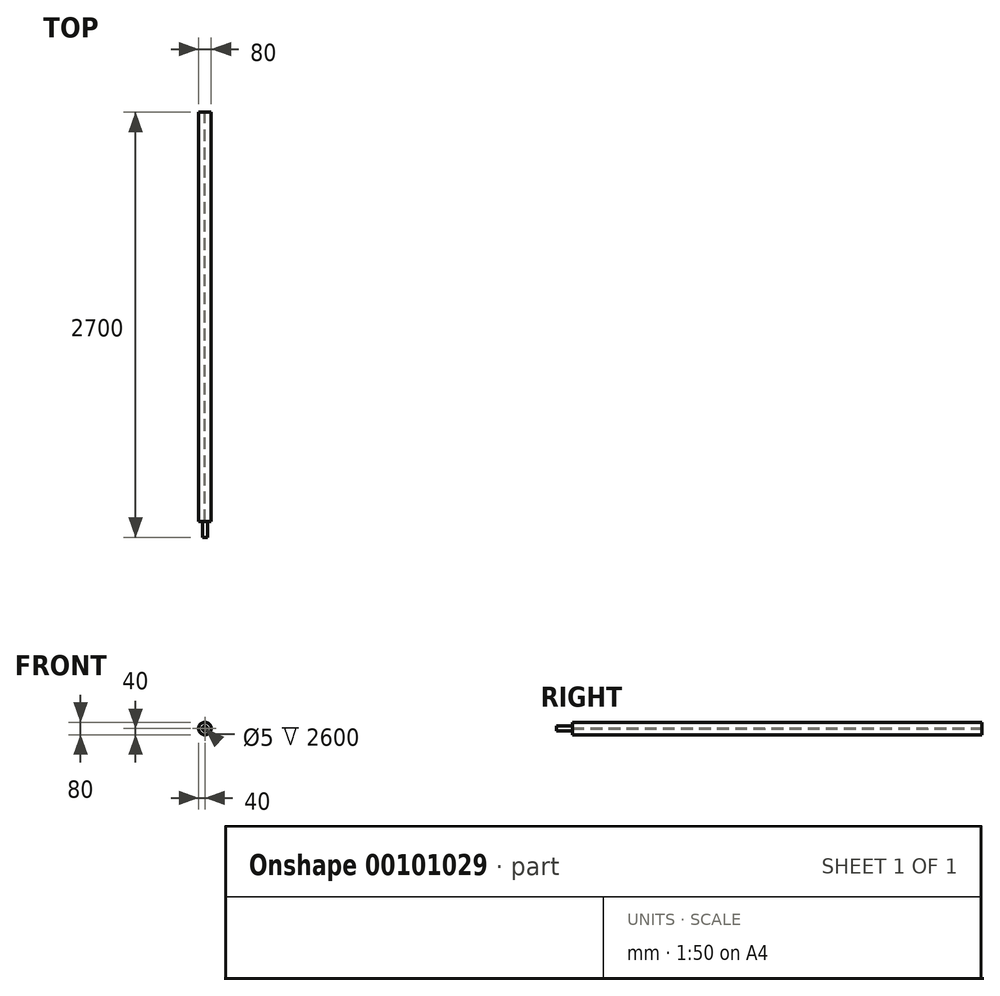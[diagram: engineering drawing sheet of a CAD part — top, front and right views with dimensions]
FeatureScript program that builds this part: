
annotation { "Feature Type Name" : "Feature", "Feature Type Description" : "" }
export const myFeature = defineFeature(function(context is Context, id is Id, definition is map)
    precondition{}
    {
        {
            var Q0;
            Q0=qCreatedBy(makeId("Front.planeOp"),FACE);
            var sketch = newSketch(context, id + "F0", { "sketchPlane" : qUnion([Q0])});
            skCircle(sketch, "E0", {"center": v(0, 0) * mm, "radius": 40 * mm});
            skCircle(sketch, "E1", {"center": v(0, 0) * mm, "radius": 2.5 * mm});
            skSolve(sketch);
        }
        {
            var Q0;
            Q0=makeQuery(id+"F0.imprint","IMPRINT",FACE,{"disambiguationData":[TD([[makeQuery(id+"F0.imprint","IMPRINT",EDGE,{"derivedFrom":sQuery(id+"F0.wireOp",EDGE,"E0")}),1.0]])]});
            extrude(context, id + "F1", {"entities" : qUnion([Q0]), "depth" : 2600 * mm});
        }
        {
            var Q0;
            Q0=makeQuery(id+"F1.opExtrude","CAP_FACE",FACE,{"disambiguationData":[OSD([sQuery(id+"F0.wireOp",EDGE,"E0"),sQuery(id+"F0.wireOp",EDGE,"E1")])],"isStart":false});
            var sketch = newSketch(context, id + "F2", { "sketchPlane" : qUnion([Q0])});
            skCircle(sketch, "E2.0", {"center": v(0, 0) * mm, "radius": 15.72 * mm});
            skSolve(sketch);
        }
        {
            var Q0;
            Q0 = qSketchRegion(id + "F2", true);
            extrude(context, id + "F3", {"entities" : qUnion([Q0]), "operationType" : NewBodyOperationType.ADD, "depth" : 100 * mm});
        }
    });
